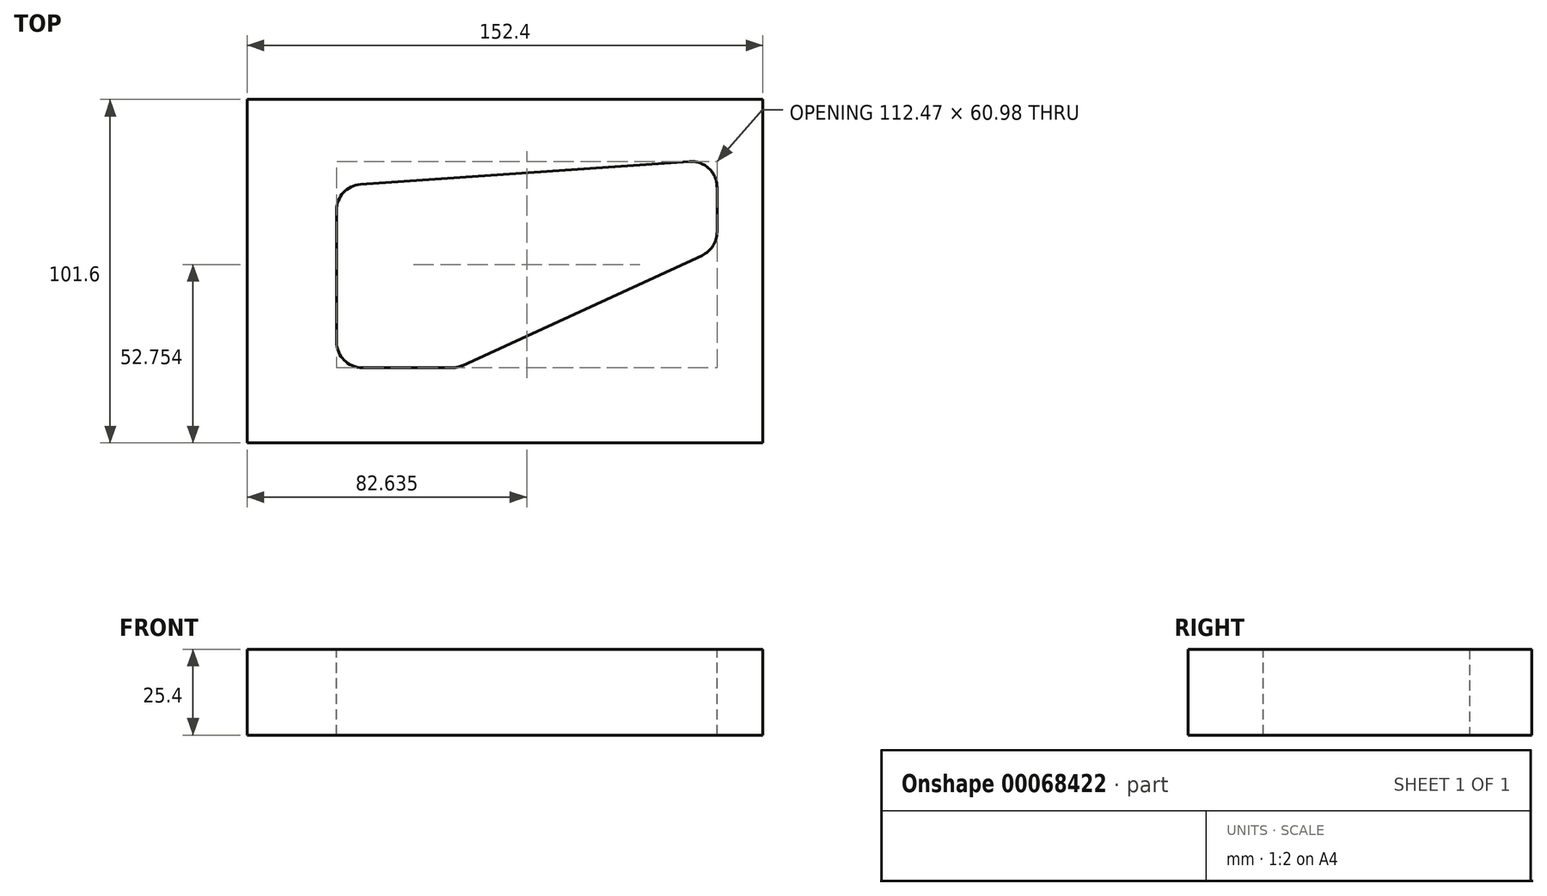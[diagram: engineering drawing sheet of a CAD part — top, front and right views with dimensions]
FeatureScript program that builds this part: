
annotation { "Feature Type Name" : "Feature", "Feature Type Description" : "" }
export const myFeature = defineFeature(function(context is Context, id is Id, definition is map)
    precondition{}
    {
        {
            var Q0;
            Q0=qCreatedBy(makeId("Top.planeOp"),FACE);
            var sketch = newSketch(context, id + "F0", { "sketchPlane" : qUnion([Q0])});
            skLineSegment(sketch, "E0.bottom", {"start": v(0, 0) * mm, "end": v(152.4, 0) * mm});
            skLineSegment(sketch, "E0.top", {"start": v(0, 101.6) * mm, "end": v(152.4, 101.6) * mm});
            skLineSegment(sketch, "E0.left", {"start": v(0, 0) * mm, "end": v(0, 101.6) * mm});
            skLineSegment(sketch, "E0.right", {"start": v(152.4, 0) * mm, "end": v(152.4, 101.6) * mm});
            skSolve(sketch);
        }
        {
            var Q0;
            Q0 = qSketchRegion(id + "F0", true);
            extrude(context, id + "F1", {"entities" : qUnion([Q0]), "depth" : 25.4 * mm});
        }
        {
            var Q0;
            Q0=makeQuery(id+"F1.opExtrude","CAP_FACE",FACE,{"disambiguationData":[OSD([sQuery(id+"F0.wireOp",EDGE,"E0.bottom"),sQuery(id+"F0.wireOp",EDGE,"E0.top"),sQuery(id+"F0.wireOp",EDGE,"E0.left"),sQuery(id+"F0.wireOp",EDGE,"E0.right")])],"isStart":false});
            var sketch = newSketch(context, id + "F2", { "sketchPlane" : qUnion([Q0])});
            skLineSegment(sketch, "E1", {"start": v(26.4, 75.98) * mm, "end": v(26.4, 22.26) * mm});
            skLineSegment(sketch, "E2", {"start": v(26.4, 22.26) * mm, "end": v(62.21, 22.26) * mm});
            skLineSegment(sketch, "E3", {"start": v(62.21, 22.26) * mm, "end": v(138.87, 57.51) * mm});
            skLineSegment(sketch, "E4", {"start": v(138.87, 57.51) * mm, "end": v(138.87, 83.81) * mm});
            skLineSegment(sketch, "E5", {"start": v(138.87, 83.81) * mm, "end": v(26.4, 75.98) * mm});
            skSolve(sketch);
        }
        {
            var Q0;
            Q0 = qSketchRegion(id + "F2", true);
            extrude(context, id + "F3", {"entities" : qUnion([Q0]), "operationType" : NewBodyOperationType.REMOVE, "oppositeDirection" : true, "depth" : 25.4 * mm});
        }
        {
            var Q0;
            Q0=makeQuery(id+"F3.boolean.opBoolean","COPY",EDGE,{"derivedFrom":makeQuery(id+"F3.opExtrude","SWEPT_EDGE",EDGE,{"disambiguationData":[OSD([sQuery(id+"F2.wireOp",EDGE,"E1"),sQuery(id+"F2.wireOp",EDGE,"E5")])]})});
            var Q1;
            Q1=makeQuery(id+"F3.boolean.opBoolean","COPY",EDGE,{"derivedFrom":makeQuery(id+"F3.opExtrude","SWEPT_EDGE",EDGE,{"disambiguationData":[OSD([sQuery(id+"F2.wireOp",EDGE,"E1"),sQuery(id+"F2.wireOp",EDGE,"E2")])]})});
            var Q2;
            Q2=makeQuery(id+"F3.boolean.opBoolean","COPY",EDGE,{"derivedFrom":makeQuery(id+"F3.opExtrude","SWEPT_EDGE",EDGE,{"disambiguationData":[OSD([sQuery(id+"F2.wireOp",EDGE,"E2"),sQuery(id+"F2.wireOp",EDGE,"E3")])]})});
            var Q3;
            Q3=makeQuery(id+"F3.boolean.opBoolean","COPY",EDGE,{"derivedFrom":makeQuery(id+"F3.opExtrude","SWEPT_EDGE",EDGE,{"disambiguationData":[OSD([sQuery(id+"F2.wireOp",EDGE,"E3"),sQuery(id+"F2.wireOp",EDGE,"E4")])]})});
            var Q4;
            Q4=makeQuery(id+"F3.boolean.opBoolean","COPY",EDGE,{"derivedFrom":makeQuery(id+"F3.opExtrude","SWEPT_EDGE",EDGE,{"disambiguationData":[OSD([sQuery(id+"F2.wireOp",EDGE,"E4"),sQuery(id+"F2.wireOp",EDGE,"E5")])]})});
            fillet(context, id + "F4", {"entities" : qUnion([Q0, Q1, Q2, Q3, Q4]), "radius" : 7.62 * mm, "tangentPropagation" : true, "allowEdgeOverflow" : false});
        }
    });
